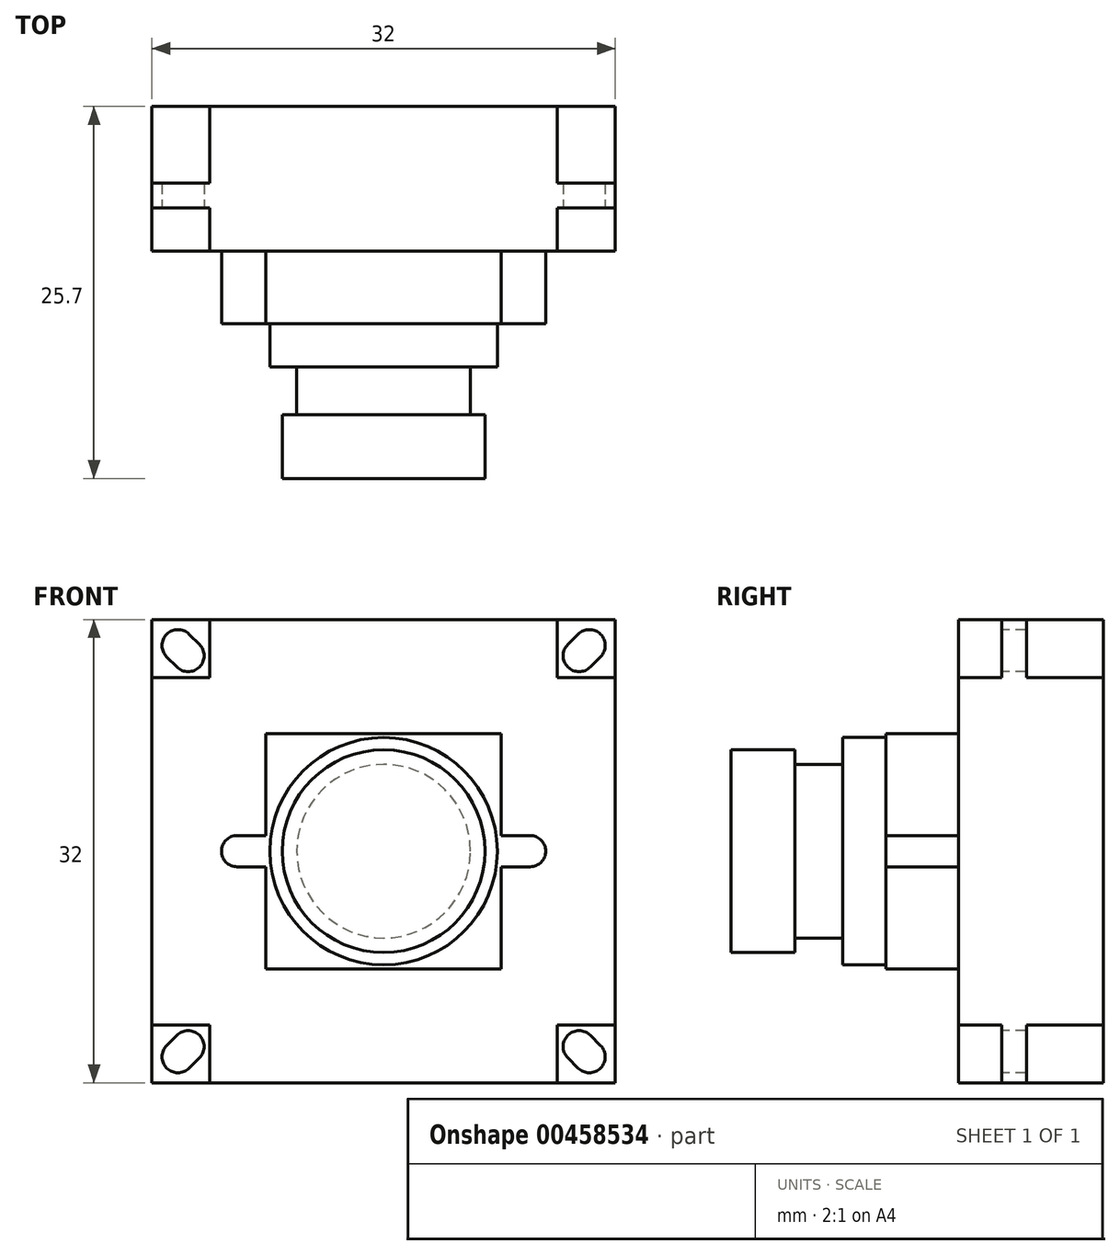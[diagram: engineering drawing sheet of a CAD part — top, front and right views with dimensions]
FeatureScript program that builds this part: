
annotation { "Feature Type Name" : "Feature", "Feature Type Description" : "" }
export const myFeature = defineFeature(function(context is Context, id is Id, definition is map)
    precondition{}
    {
        {
            var Q0;
            Q0=qCreatedBy(makeId("Front.planeOp"),FACE);
            var sketch = newSketch(context, id + "F0", { "sketchPlane" : qUnion([Q0])});
            skLineSegment(sketch, "E0.bottom", {"start": v(-16, 16) * mm, "end": v(16, 16) * mm});
            skLineSegment(sketch, "E0.top", {"start": v(-16, -16) * mm, "end": v(16, -16) * mm});
            skLineSegment(sketch, "E0.left", {"start": v(-16, 16) * mm, "end": v(-16, -16) * mm});
            skLineSegment(sketch, "E0.right", {"start": v(16, 16) * mm, "end": v(16, -16) * mm});
            skPoint(sketch, "E0.middle", {"position": v(0, 0) * mm});
            skSolve(sketch);
        }
        {
            var Q0;
            Q0=qSketchRegion(id+"F0",true);
            extrude(context, id + "F1", {"entities" : qUnion([Q0]), "depth" : 1.7 * mm});
        }
        {
            var Q0;
            Q0=makeQuery(id+"F1.opExtrude","CAP_FACE",FACE,{"disambiguationData":[OSD([sQuery(id+"F0.wireOp",EDGE,"E0.bottom"),sQuery(id+"F0.wireOp",EDGE,"E0.top"),sQuery(id+"F0.wireOp",EDGE,"E0.left"),sQuery(id+"F0.wireOp",EDGE,"E0.right")])],"isStart":false});
            var sketch = newSketch(context, id + "F2", { "sketchPlane" : qUnion([Q0])});
            skLineSegment(sketch, "E1.bottom", {"start": v(-16, -16) * mm, "end": v(-12, -16) * mm, "construction": true});
            skLineSegment(sketch, "E1.top", {"start": v(-16, -12) * mm, "end": v(-12, -12) * mm});
            skLineSegment(sketch, "E1.left", {"start": v(-16, -16) * mm, "end": v(-16, -12) * mm, "construction": true});
            skLineSegment(sketch, "E1.right", {"start": v(-12, -16) * mm, "end": v(-12, -12) * mm});
            skLineSegment(sketch, "E2.MirrorCS", {"start": v(16, -12) * mm, "end": v(12, -12) * mm});
            skLineSegment(sketch, "E3.MirrorCS", {"start": v(12, -16) * mm, "end": v(12, -12) * mm});
            skLineSegment(sketch, "E4.MirrorCS", {"start": v(-16, 12) * mm, "end": v(-12, 12) * mm});
            skLineSegment(sketch, "E5.MirrorCS", {"start": v(-12, 16) * mm, "end": v(-12, 12) * mm});
            skLineSegment(sketch, "E6.MirrorCS", {"start": v(16, 12) * mm, "end": v(12, 12) * mm});
            skLineSegment(sketch, "E7.MirrorCS", {"start": v(12, 16) * mm, "end": v(12, 12) * mm});
            skLineSegment(sketch, "E8", {"start": v(-12, -16) * mm, "end": v(12, -16) * mm});
            skLineSegment(sketch, "E9", {"start": v(16, -12) * mm, "end": v(16, 12) * mm});
            skLineSegment(sketch, "E10", {"start": v(12, 16) * mm, "end": v(-12, 16) * mm});
            skLineSegment(sketch, "E11", {"start": v(-16, 12) * mm, "end": v(-16, -12) * mm});
            skSolve(sketch);
        }
        {
            var Q0;
            Q0=makeQuery(id+"F2.imprint","IMPRINT",FACE,{"disambiguationData":[TD([[makeQuery(id+"F2.imprint","IMPRINT",EDGE,{"derivedFrom":sQuery(id+"F2.wireOp",EDGE,"E1.top")}),1.0]])]});
            extrude(context, id + "F3", {"entities" : qUnion([Q0]), "operationType" : NewBodyOperationType.ADD, "depth" : 3 * mm});
        }
        {
            var Q0;
            Q0=makeQuery(id+"F3.opExtrude","CAP_FACE",FACE,{"disambiguationData":[OSD([sQuery(id+"F2.wireOp",EDGE,"E1.top"),sQuery(id+"F2.wireOp",EDGE,"E1.right"),sQuery(id+"F2.wireOp",EDGE,"E2.MirrorCS"),sQuery(id+"F2.wireOp",EDGE,"E3.MirrorCS"),sQuery(id+"F2.wireOp",EDGE,"E4.MirrorCS"),sQuery(id+"F2.wireOp",EDGE,"E5.MirrorCS"),sQuery(id+"F2.wireOp",EDGE,"E6.MirrorCS"),sQuery(id+"F2.wireOp",EDGE,"E7.MirrorCS"),sQuery(id+"F2.wireOp",EDGE,"E8"),sQuery(id+"F2.wireOp",EDGE,"E9"),sQuery(id+"F2.wireOp",EDGE,"E10"),sQuery(id+"F2.wireOp",EDGE,"E11")])],"isStart":false});
            var sketch = newSketch(context, id + "F4", { "sketchPlane" : qUnion([Q0])});
            skLineSegment(sketch, "E12.bottom", {"start": v(-8.12, 8.12) * mm, "end": v(8.12, 8.12) * mm});
            skLineSegment(sketch, "E12.top", {"start": v(-8.12, -8.13) * mm, "end": v(8.12, -8.13) * mm});
            skLineSegment(sketch, "E12.left", {"start": v(-8.13, 8.12) * mm, "end": v(-8.12, -8.12) * mm});
            skLineSegment(sketch, "E12.right", {"start": v(8.12, 8.12) * mm, "end": v(8.13, -8.12) * mm});
            skLineSegment(sketch, "E13", {"start": v(-8.12, 0) * mm, "end": v(-10.12, 0) * mm, "construction": true});
            skPoint(sketch, "E13.endSnap0", {"position": v(-8.12, 0) * mm});
            skLineSegment(sketch, "E14", {"start": v(8.12, 0) * mm, "end": v(10.12, 0) * mm, "construction": true});
            skPoint(sketch, "E14.endSnap0", {"position": v(8.12, 0) * mm});
            skArc(sketch, "E15.0.startCap", {"start": v(-8.12, 1.07) * mm, "mid": v(-7.05, 0) * mm, "end": v(-8.12, -1.08) * mm});
            skArc(sketch, "E15.0.endCap", {"start": v(-10.12, -1.08) * mm, "mid": v(-11.2, 0) * mm, "end": v(-10.12, 1.07) * mm});
            skLineSegment(sketch, "E15.0.left", {"start": v(-8.12, -1.07) * mm, "end": v(-10.12, -1.08) * mm});
            skLineSegment(sketch, "E15.0.right", {"start": v(-8.12, 1.07) * mm, "end": v(-10.12, 1.07) * mm});
            skArc(sketch, "E16.0.startCap", {"start": v(8.12, -1.07) * mm, "mid": v(7.05, 0) * mm, "end": v(8.12, 1.08) * mm});
            skArc(sketch, "E16.0.endCap", {"start": v(10.12, 1.07) * mm, "mid": v(11.2, 0) * mm, "end": v(10.12, -1.07) * mm});
            skLineSegment(sketch, "E16.0.left", {"start": v(8.12, 1.07) * mm, "end": v(10.12, 1.07) * mm});
            skLineSegment(sketch, "E16.0.right", {"start": v(8.12, -1.07) * mm, "end": v(10.12, -1.07) * mm});
            skSolve(sketch);
        }
        {
            var Q0;
            Q0=qSketchRegion(id+"F4",true);
            extrude(context, id + "F5", {"entities" : qUnion([Q0]), "operationType" : NewBodyOperationType.ADD, "depth" : 5 * mm});
        }
        {
            var Q0;
            Q0=makeQuery(id+"F5.opExtrude","CAP_FACE",FACE,{"disambiguationData":[OSD([sQuery(id+"F4.wireOp",EDGE,"E12.bottom"),sQuery(id+"F4.wireOp",EDGE,"E12.top"),sQuery(id+"F4.wireOp",EDGE,"E12.left"),sQuery(id+"F4.wireOp",EDGE,"E12.right"),sQuery(id+"F4.wireOp",EDGE,"E15.0.endCap"),sQuery(id+"F4.wireOp",EDGE,"E15.0.left"),sQuery(id+"F4.wireOp",EDGE,"E15.0.right"),sQuery(id+"F4.wireOp",EDGE,"E16.0.endCap"),sQuery(id+"F4.wireOp",EDGE,"E16.0.left"),sQuery(id+"F4.wireOp",EDGE,"E16.0.right")])],"isStart":false});
            var sketch = newSketch(context, id + "F6", { "sketchPlane" : qUnion([Q0])});
            skCircle(sketch, "E17", {"center": v(0, 0) * mm, "radius": 7.85 * mm});
            skSolve(sketch);
        }
        {
            var Q0;
            Q0=qSketchRegion(id+"F6",true);
            extrude(context, id + "F7", {"entities" : qUnion([Q0]), "operationType" : NewBodyOperationType.ADD, "depth" : 3 * mm});
        }
        {
            var Q0;
            Q0=makeQuery(id+"F7.opExtrude","CAP_FACE",FACE,{"disambiguationData":[OSD([sQuery(id+"F6.wireOp",EDGE,"E17")])],"isStart":false});
            var sketch = newSketch(context, id + "F8", { "sketchPlane" : qUnion([Q0])});
            skCircle(sketch, "E18", {"center": v(0, 0) * mm, "radius": 6 * mm});
            skSolve(sketch);
        }
        {
            var Q0;
            Q0=qSketchRegion(id+"F8",true);
            extrude(context, id + "F9", {"entities" : qUnion([Q0]), "operationType" : NewBodyOperationType.ADD, "depth" : 3.3 * mm});
        }
        {
            var Q0;
            Q0=makeQuery(id+"F9.opExtrude","CAP_FACE",FACE,{"disambiguationData":[OSD([sQuery(id+"F8.wireOp",EDGE,"E18")])],"isStart":false});
            var sketch = newSketch(context, id + "F10", { "sketchPlane" : qUnion([Q0])});
            skCircle(sketch, "E19", {"center": v(0, 0) * mm, "radius": 7 * mm});
            skSolve(sketch);
        }
        {
            var Q0;
            Q0=qSketchRegion(id+"F10",true);
            extrude(context, id + "F11", {"entities" : qUnion([Q0]), "operationType" : NewBodyOperationType.ADD, "depth" : 4.4 * mm});
        }
        {
            var Q0;
            Q0=makeQuery(id+"F1.opExtrude","CAP_FACE",FACE,{"disambiguationData":[OSD([sQuery(id+"F0.wireOp",EDGE,"E0.bottom"),sQuery(id+"F0.wireOp",EDGE,"E0.top"),sQuery(id+"F0.wireOp",EDGE,"E0.left"),sQuery(id+"F0.wireOp",EDGE,"E0.right")])],"isStart":true});
            var sketch = newSketch(context, id + "F12", { "sketchPlane" : qUnion([Q0])});
            skLineSegment(sketch, "E20.top", {"start": v(-16, 12) * mm, "end": v(-12, 12) * mm});
            skLineSegment(sketch, "E20.right", {"start": v(-12, 16) * mm, "end": v(-12, 12) * mm});
            skLineSegment(sketch, "E21.MirrorCS", {"start": v(12, 16) * mm, "end": v(12, 12) * mm});
            skLineSegment(sketch, "E22.MirrorCS", {"start": v(16, 12) * mm, "end": v(12, 12) * mm});
            skLineSegment(sketch, "E23.MirrorCS", {"start": v(16, -12) * mm, "end": v(12, -12) * mm});
            skLineSegment(sketch, "E24.MirrorCS", {"start": v(12, -16) * mm, "end": v(12, -12) * mm});
            skLineSegment(sketch, "E25.MirrorCS", {"start": v(-16, -12) * mm, "end": v(-12, -12) * mm});
            skLineSegment(sketch, "E26.MirrorCS", {"start": v(-12, -16) * mm, "end": v(-12, -12) * mm});
            skLineSegment(sketch, "E27", {"start": v(-12, 16) * mm, "end": v(12, 16) * mm});
            skLineSegment(sketch, "E28", {"start": v(16, 12) * mm, "end": v(16, -12) * mm});
            skLineSegment(sketch, "E29", {"start": v(12, -16) * mm, "end": v(-12, -16) * mm});
            skLineSegment(sketch, "E30", {"start": v(-16, -12) * mm, "end": v(-16, 12) * mm});
            skSolve(sketch);
        }
        {
            var Q0;
            Q0=qSketchRegion(id+"F12",true);
            extrude(context, id + "F13", {"entities" : qUnion([Q0]), "operationType" : NewBodyOperationType.ADD, "depth" : 5.3 * mm});
        }
        {
            var Q0;
            {var subQ0=sQuery(id+"F0.wireOp",EDGE,"E0.left");var subQ1=sQuery(id+"F0.wireOp",EDGE,"E0.bottom");Q0=makeQuery(id+"F3.boolean.opBoolean","SPLIT",FACE,{"disambiguationData":[TD([makeQuery(id+"F3.opExtrude","SWEPT_FACE",FACE,{"disambiguationData":[OSD([sQuery(id+"F2.wireOp",EDGE,"E4.MirrorCS")])]})])],"derivedFrom":makeQuery(id+"F1.opExtrude","CAP_FACE",FACE,{"disambiguationData":[OSD([subQ1,sQuery(id+"F0.wireOp",EDGE,"E0.top"),subQ0,sQuery(id+"F0.wireOp",EDGE,"E0.right")])],"isStart":false})});}
            var sketch = newSketch(context, id + "F14", { "sketchPlane" : qUnion([Q0])});
            skLineSegment(sketch, "E31", {"start": v(-13.5, 13.5) * mm, "end": v(-14.2, 14.2) * mm});
            skLineSegment(sketch, "E32", {"start": v(-13.5, 13.5) * mm, "end": v(0, 13.5) * mm, "construction": true});
            skLineSegment(sketch, "E33", {"start": v(-13.5, 13.5) * mm, "end": v(-13.5, 0) * mm, "construction": true});
            skArc(sketch, "E34.0.startCap", {"start": v(-12.72, 14.28) * mm, "mid": v(-12.72, 12.72) * mm, "end": v(-14.28, 12.72) * mm});
            skArc(sketch, "E34.0.endCap", {"start": v(-14.98, 13.43) * mm, "mid": v(-14.98, 14.98) * mm, "end": v(-13.43, 14.98) * mm});
            skLineSegment(sketch, "E34.0.left", {"start": v(-14.28, 12.72) * mm, "end": v(-14.98, 13.43) * mm});
            skLineSegment(sketch, "E34.0.right", {"start": v(-12.72, 14.28) * mm, "end": v(-13.43, 14.98) * mm});
            skLineSegment(sketch, "E35.MirrorCS", {"start": v(12.72, 14.28) * mm, "end": v(13.43, 14.98) * mm});
            skLineSegment(sketch, "E36.MirrorCS", {"start": v(14.28, 12.72) * mm, "end": v(14.98, 13.43) * mm});
            skArc(sketch, "E37.MirrorCS", {"start": v(12.72, 14.28) * mm, "mid": v(12.72, 12.72) * mm, "end": v(14.28, 12.72) * mm});
            skArc(sketch, "E38.MirrorCS", {"start": v(14.98, 13.43) * mm, "mid": v(14.98, 14.98) * mm, "end": v(13.43, 14.98) * mm});
            skLineSegment(sketch, "E39.MirrorCS", {"start": v(14.28, -12.72) * mm, "end": v(14.98, -13.43) * mm});
            skArc(sketch, "E40.MirrorCS", {"start": v(14.98, -13.43) * mm, "mid": v(14.98, -14.98) * mm, "end": v(13.43, -14.98) * mm});
            skLineSegment(sketch, "E41.MirrorCS", {"start": v(12.72, -14.28) * mm, "end": v(13.43, -14.98) * mm});
            skArc(sketch, "E42.MirrorCS", {"start": v(12.72, -14.28) * mm, "mid": v(12.72, -12.72) * mm, "end": v(14.28, -12.72) * mm});
            skLineSegment(sketch, "E43.MirrorCS", {"start": v(-12.72, -14.28) * mm, "end": v(-13.43, -14.98) * mm});
            skLineSegment(sketch, "E44.MirrorCS", {"start": v(-14.28, -12.72) * mm, "end": v(-14.98, -13.43) * mm});
            skArc(sketch, "E45.MirrorCS", {"start": v(-12.72, -14.28) * mm, "mid": v(-12.72, -12.72) * mm, "end": v(-14.28, -12.72) * mm});
            skArc(sketch, "E46.MirrorCS", {"start": v(-14.98, -13.43) * mm, "mid": v(-14.98, -14.98) * mm, "end": v(-13.43, -14.98) * mm});
            skSolve(sketch);
        }
        {
            var Q0;
            Q0=qSketchRegion(id+"F14",true);
            extrude(context, id + "F15", {"entities" : qUnion([Q0]), "operationType" : NewBodyOperationType.REMOVE, "oppositeDirection" : true, "depth" : 2 * mm});
        }
    });
